# Revit family: 65QBC,QMC,QHC_SET_231217_1
name_source: partatom
category: 통신 장치
units: mm (PartAtom-declared; Revit-internal decimal feet)

## family parameters
OmniClass 번호 = 23.85.10.14.24
OmniClass 제목 = Video Monitors
공유 = 아니오
로드될 때 보이드를 사용하여 절단 = 아니오
룸 계산 점 = 아니오
부품 유형 = 보통
원형 커넥터 치수 = 지름 사용
작업 기준면 기반 = 아니오
주석 방향을 유지합니다. = 아니오
항상 수직 = 예

## types (3) — shared parameters
Active Display Area = 1428.48(H) x 803.52(V)
Bezel Width (mm) = 11.5  [stored 0.0377297 ft]
Color Gamut = NTSC 72%
Contrast Ratio (Typ.) = 4,000:1
Diagonal Size (Class) = 65  [stored 0.213255 ft]
Diagonal Size (Measured) = 64.5
Dimension Package (mm) = TBD
Dimension Set (mm) = 1456.8 x 831.9 x 28.5
Dimension Set Depth (mm) = 28.5  [stored 0.0935039 ft]
Dimension Set Height (mm) = 831.9  [stored 2.72933 ft]
Dimension Set Width (mm) = 1456.8  [stored 4.77953 ft]
EMC = Class B
Environment = ENERGY STAR 8.0, EPEAT
External Control = RS232C(In/Out),RJ45
IP Rating = IP5x
Input USB = USB 2.0 x 2
Internal Operating System = Tizen 7.0
Key = UHD Signage with Built-in MagicInfoS10, SSSP10.0
Optional Mount = WMN-B50SC
Optional Specialty = TBD
Optional Stand = STN-L6585C
Orientation = Landscape/Portrait
Output Audio = Stereo mini Jack
Pixel Pitch (mm) = 0.372 x 0.372
Power Consumption Max [W/h] = TBD
Power Consumption Sleep mode = less than 0.5W
Power Consumption Typical [W/h] = TBD
Power Supply = AC100 - 240V, 50/60 Hz
Relative Humidity = 10~80%
Resolution = 3840 x 2160 (16:9)
Safety = 60950-1/62368-1
Screen = Samsung Electronics Screen
Security = 802.1 x (WPA2 Enterprise) : EAP-TLS, EAP-TTLS, EAP-PEAP
Speaker = 10W 2ch
Temperature = 0℃ ~ 40℃
Type = VA
VESA Mount = 400 x 300
VESA Mount Screw (Min-Max) = M8, 12-14mm
Weight Package (kg) = TBD
Weight Set (kg) = TBD
WiFi/BT = O/O
제조업체 = Samsung Electronics Co., Ltd.
조합 코드 = E1020500
키노트 = 11 52 00

## per-type parameters (varying)
| type | Brightness (Typ.) | Haze | Input Video | Internal Processor | Internal Storage (FDM) | Operation Hour |
| UHD Signage QB65C | 350 nit | 2% | HDMI 2.0(3) | CA53 1.3GHz Quad-Core | 8GB (3GB available) | 16/7 |
| UHD Signage QM65C | 500 nit | 25% | DP1.2(1), HDMI 2.0(3) | CA73 1.6GHz Quad-Core | 16GB (10GB available) | 24/7 |
| UHD Signage QH65C | 700 nit | 25% | DP1.2(1), HDMI 2.0(3) | CA73 1.6GHz Quad-Core | 16GB (10GB available) | 24/7 |

note: column(s) folded — value = type name in every type: 모델

note: [stored X ft] marks values corroborated as IEEE doubles in the binary element streams (Revit-internal decimal feet)
